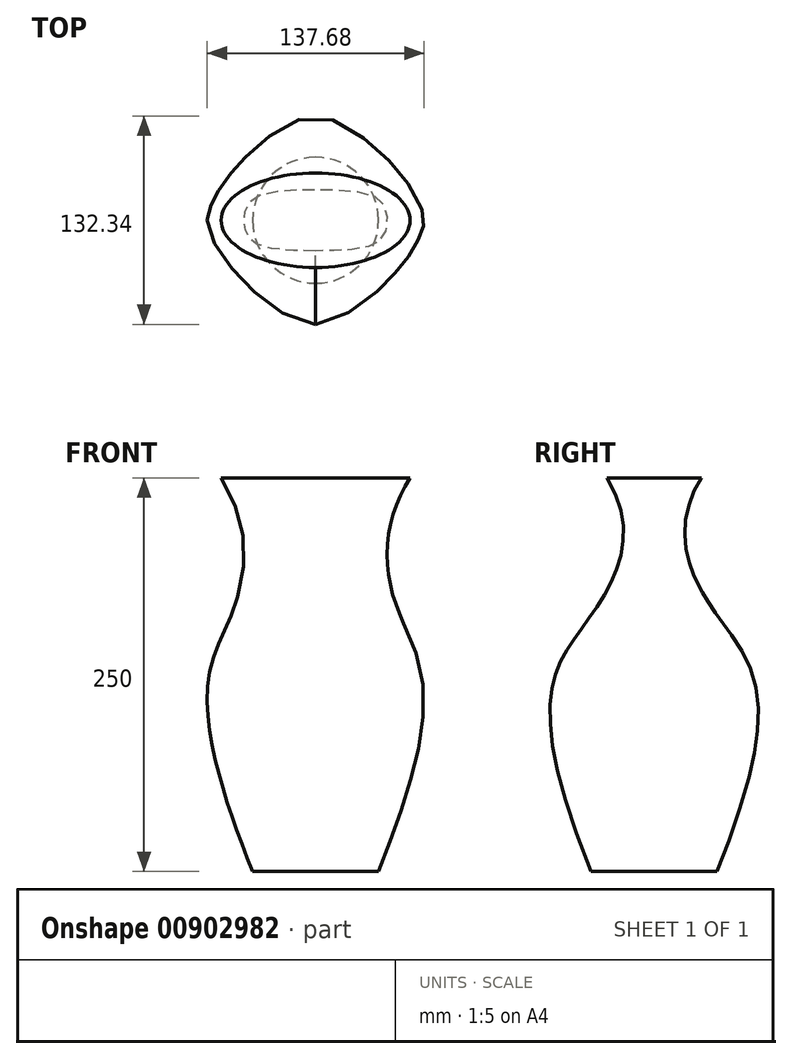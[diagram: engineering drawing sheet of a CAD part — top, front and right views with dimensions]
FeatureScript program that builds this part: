
annotation { "Feature Type Name" : "Feature", "Feature Type Description" : "" }
export const myFeature = defineFeature(function(context is Context, id is Id, definition is map)
    precondition{}
    {
        {
            var Q0;
            Q0=qCreatedBy(makeId("Top.planeOp"),FACE);
            var sketch = newSketch(context, id + "F0", { "sketchPlane" : qUnion([Q0])});
            skCircle(sketch, "E0", {"center": v(0, 0) * mm, "radius": 40 * mm});
            skSolve(sketch);
        }
        {
            var Q0;
            Q0=qCreatedBy(makeId("Top.planeOp"),FACE);
            cPlane(context, id + "F1", {"entities" : qUnion([Q0]), "cplaneType" : CPlaneType.OFFSET, "offset" : 250 * mm, "width" : 150 * mm, "height" : 150 * mm});
        }
        {
            var Q0;
            Q0=qCreatedBy(id+"F1.planeOp",FACE);
            var sketch = newSketch(context, id + "F2", { "sketchPlane" : qUnion([Q0])});
            skEllipse(sketch, "E1", {"center": v(0, 0) * mm, "majorRadius": 60 * mm, "minorRadius": 30 * mm, "majorAxis": v(1, 0)});
            skSolve(sketch);
        }
        {
            var Q0;
            Q0=qCreatedBy(makeId("Front.planeOp"),FACE);
            var sketch = newSketch(context, id + "F3", { "sketchPlane" : qUnion([Q0])});
            skFitSpline(sketch, "E2", {"points": [v(-40, 0) * mm, v(-53.68, 162.67) * mm, v(-60, 250) * mm], "startDerivative": vector(-238.02, 591.95) * mm, "endDerivative": vector(-151.95, 245.46) * mm});
            skFitSpline(sketch, "E3.MirrorCS", {"points": [v(40, 0) * mm, v(53.68, 162.67) * mm, v(60, 250) * mm], "startDerivative": vector(238.02, 591.95) * mm, "endDerivative": vector(151.95, 245.46) * mm});
            skSolve(sketch);
        }
        {
            var Q0;
            Q0=qCreatedBy(makeId("Right.planeOp"),FACE);
            var sketch = newSketch(context, id + "F4", { "sketchPlane" : qUnion([Q0])});
            skFitSpline(sketch, "E4", {"points": [v(-40, 0) * mm, v(-40, 162.67) * mm, v(-30, 250) * mm], "startDerivative": vector(-238.4, 592.88) * mm, "endDerivative": vector(-151.62, 244.93) * mm});
            skFitSpline(sketch, "E5.MirrorCS", {"points": [v(40, 0) * mm, v(40, 162.67) * mm, v(30, 250) * mm], "startDerivative": vector(238.4, 592.88) * mm, "endDerivative": vector(151.62, 244.93) * mm});
            skSolve(sketch);
        }
        {
            var Q0;
            Q0=makeQuery(id+"F0.imprint","IMPRINT",FACE,{"disambiguationData":[TD([[makeQuery(id+"F0.imprint","IMPRINT",EDGE,{"derivedFrom":sQuery(id+"F0.wireOp",EDGE,"E0")}),1.0]])]});
            var Q1;
            Q1=makeQuery(id+"F2.imprint","IMPRINT",FACE,{"disambiguationData":[TD([[makeQuery(id+"F2.imprint","IMPRINT",EDGE,{"derivedFrom":sQuery(id+"F2.wireOp",EDGE,"E1")}),1.0]])]});
            var Q2;
            Q2=sQuery(id+"F4.wireOp",EDGE,"E4");
            var Q3;
            Q3=sQuery(id+"F3.wireOp",EDGE,"E2");
            var Q4;
            Q4=sQuery(id+"F4.wireOp",EDGE,"E5.MirrorCS");
            var Q5;
            Q5=sQuery(id+"F3.wireOp",EDGE,"E3.MirrorCS");
            loft(context, id + "F5", {"addGuides" : true, "sheetProfilesArray" : [{ "sheetProfileEntities" : qUnion([Q0]) }, { "sheetProfileEntities" : qUnion([Q1]) }], "guidesArray" : [{ "guideEntities" : qUnion([Q2]), "guideDerivativeType" : LoftGuideDerivativeType.DEFAULT, "guideDerivativeMagnitude" : 1 }, { "guideEntities" : qUnion([Q3]), "guideDerivativeType" : LoftGuideDerivativeType.DEFAULT, "guideDerivativeMagnitude" : 1 }, { "guideEntities" : qUnion([Q4]), "guideDerivativeType" : LoftGuideDerivativeType.DEFAULT, "guideDerivativeMagnitude" : 1 }, { "guideEntities" : qUnion([Q5]), "guideDerivativeType" : LoftGuideDerivativeType.DEFAULT, "guideDerivativeMagnitude" : 1 }]});
        }
    });
